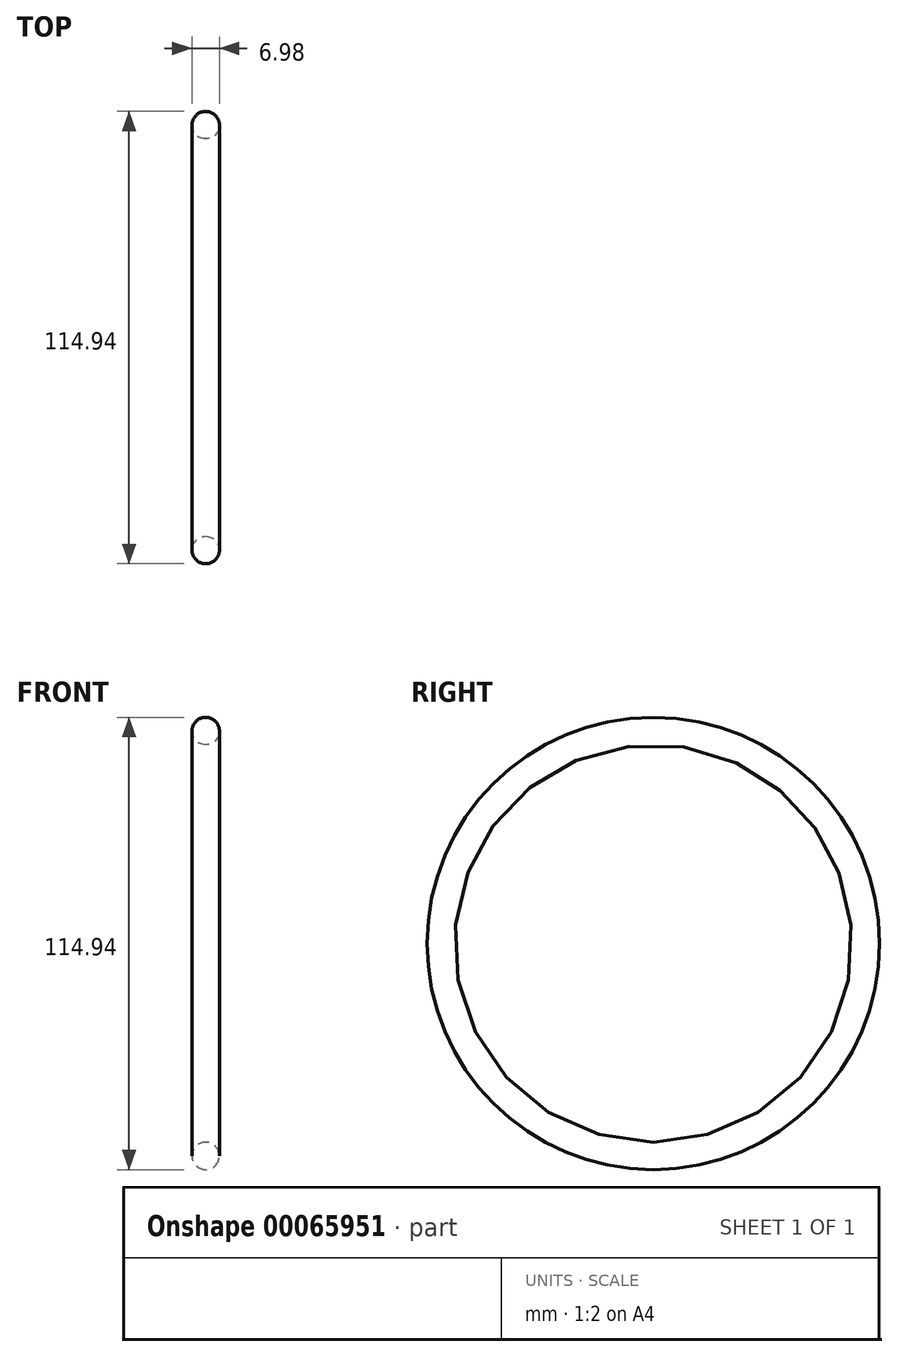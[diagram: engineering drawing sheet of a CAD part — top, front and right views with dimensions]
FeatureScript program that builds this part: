
annotation { "Feature Type Name" : "Feature", "Feature Type Description" : "" }
export const myFeature = defineFeature(function(context is Context, id is Id, definition is map)
    precondition{}
    {
        {
            var Q0;
            Q0=qCreatedBy(makeId("Front.planeOp"),FACE);
            var sketch = newSketch(context, id + "F0", { "sketchPlane" : qUnion([Q0])});
            skLineSegment(sketch, "E0", {"start": v(0, 0) * mm, "end": v(-6.06, 0) * mm, "construction": true});
            skCircle(sketch, "E1", {"center": v(0, 53.98) * mm, "radius": 3.5 * mm});
            skSolve(sketch);
        }
        {
            var Q0;
            Q0=makeQuery(id+"F0.imprint","IMPRINT",FACE,{"disambiguationData":[TD([[makeQuery(id+"F0.imprint","IMPRINT",EDGE,{"derivedFrom":sQuery(id+"F0.wireOp",EDGE,"E1")}),1.0]])]});
            var Q1;
            Q1=sQuery(id+"F0.wireOp",EDGE,"E0");
            revolve(context, id + "F1", {"entities" : qUnion([Q0]), "axis" : qUnion([Q1]), "revolveType" : RevolveType.FULL});
        }
    });
